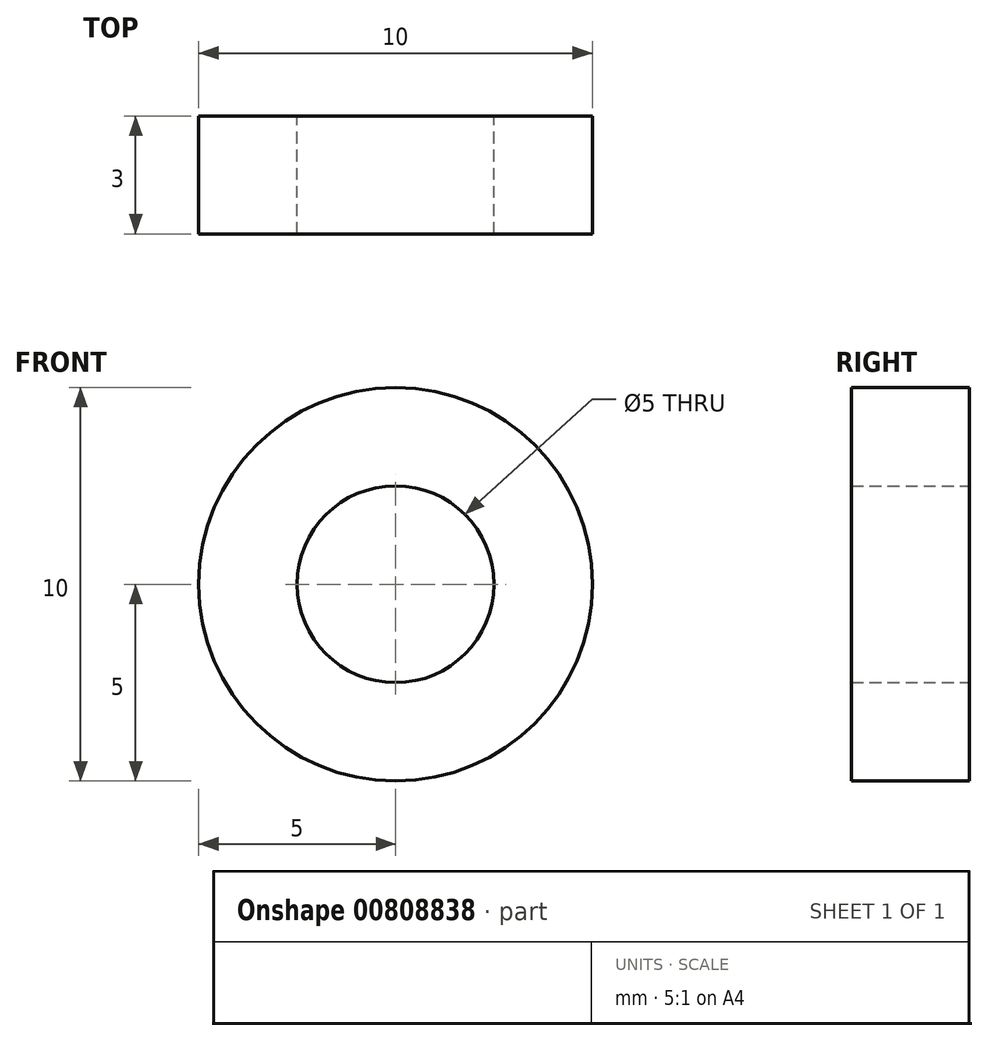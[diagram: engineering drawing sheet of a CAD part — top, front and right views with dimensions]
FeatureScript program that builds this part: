
annotation { "Feature Type Name" : "Feature", "Feature Type Description" : "" }
export const myFeature = defineFeature(function(context is Context, id is Id, definition is map)
    precondition{}
    {
        {
            var Q0;
            Q0=qCreatedBy(makeId("Front.planeOp"),FACE);
            var sketch = newSketch(context, id + "F0", { "sketchPlane" : qUnion([Q0])});
            skCircle(sketch, "E0", {"center": v(0, 0) * mm, "radius": 5 * mm});
            skCircle(sketch, "E1", {"center": v(0, 0) * mm, "radius": 2.5 * mm});
            skSolve(sketch);
        }
        {
            var Q0;
            Q0=qSketchRegion(id+"F0",true);
            extrude(context, id + "F1", {"entities" : qUnion([Q0]), "depth" : 3 * mm, "offsetDistance" : 25 * mm});
        }
    });
